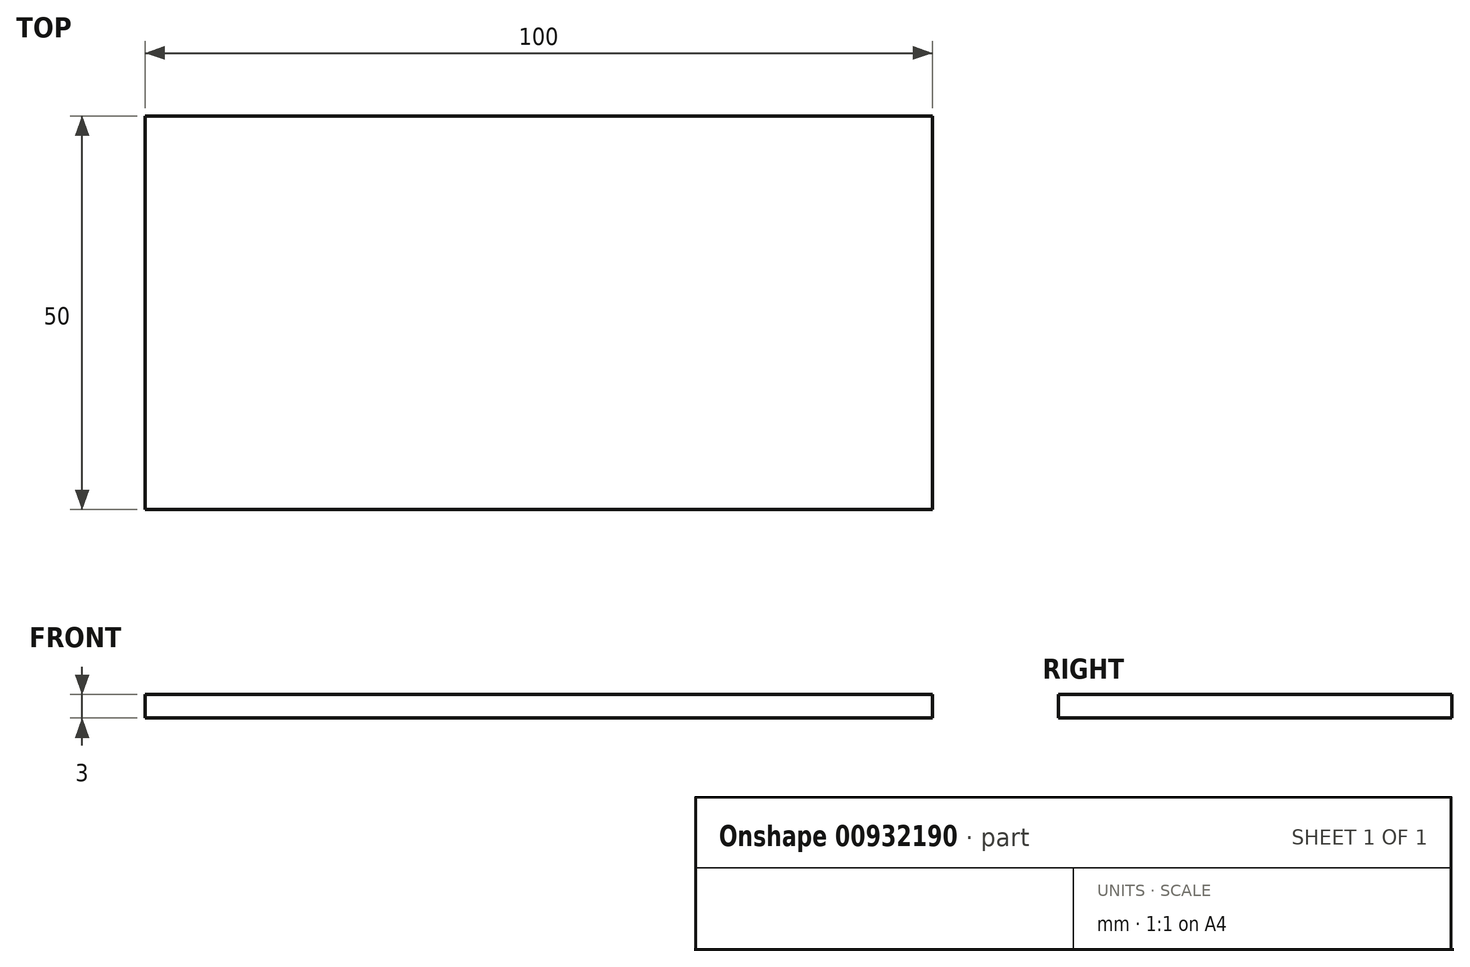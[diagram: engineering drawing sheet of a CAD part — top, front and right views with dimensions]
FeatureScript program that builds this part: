
annotation { "Feature Type Name" : "Feature", "Feature Type Description" : "" }
export const myFeature = defineFeature(function(context is Context, id is Id, definition is map)
    precondition{}
    {
        {
            var Q0;
            Q0=qCreatedBy(makeId("Top.planeOp"),FACE);
            var sketch = newSketch(context, id + "F0", { "sketchPlane" : qUnion([Q0])});
            skLineSegment(sketch, "E0.bottom", {"start": v(0, 0) * mm, "end": v(100, 0) * mm});
            skLineSegment(sketch, "E0.top", {"start": v(0, 50) * mm, "end": v(100, 50) * mm});
            skLineSegment(sketch, "E0.left", {"start": v(0, 0) * mm, "end": v(0, 50) * mm});
            skLineSegment(sketch, "E0.right", {"start": v(100, 0) * mm, "end": v(100, 50) * mm});
            skSolve(sketch);
        }
        {
            var Q0;
            Q0=makeQuery(id+"F0.imprint","IMPRINT",FACE,{"disambiguationData":[TD([[makeQuery(id+"F0.imprint","IMPRINT",EDGE,{"derivedFrom":sQuery(id+"F0.wireOp",EDGE,"E0.bottom")}),1.0]])]});
            extrude(context, id + "F1", {"entities" : qUnion([Q0]), "depth" : 3 * mm, "offsetDistance" : 25.4 * mm});
        }
    });
